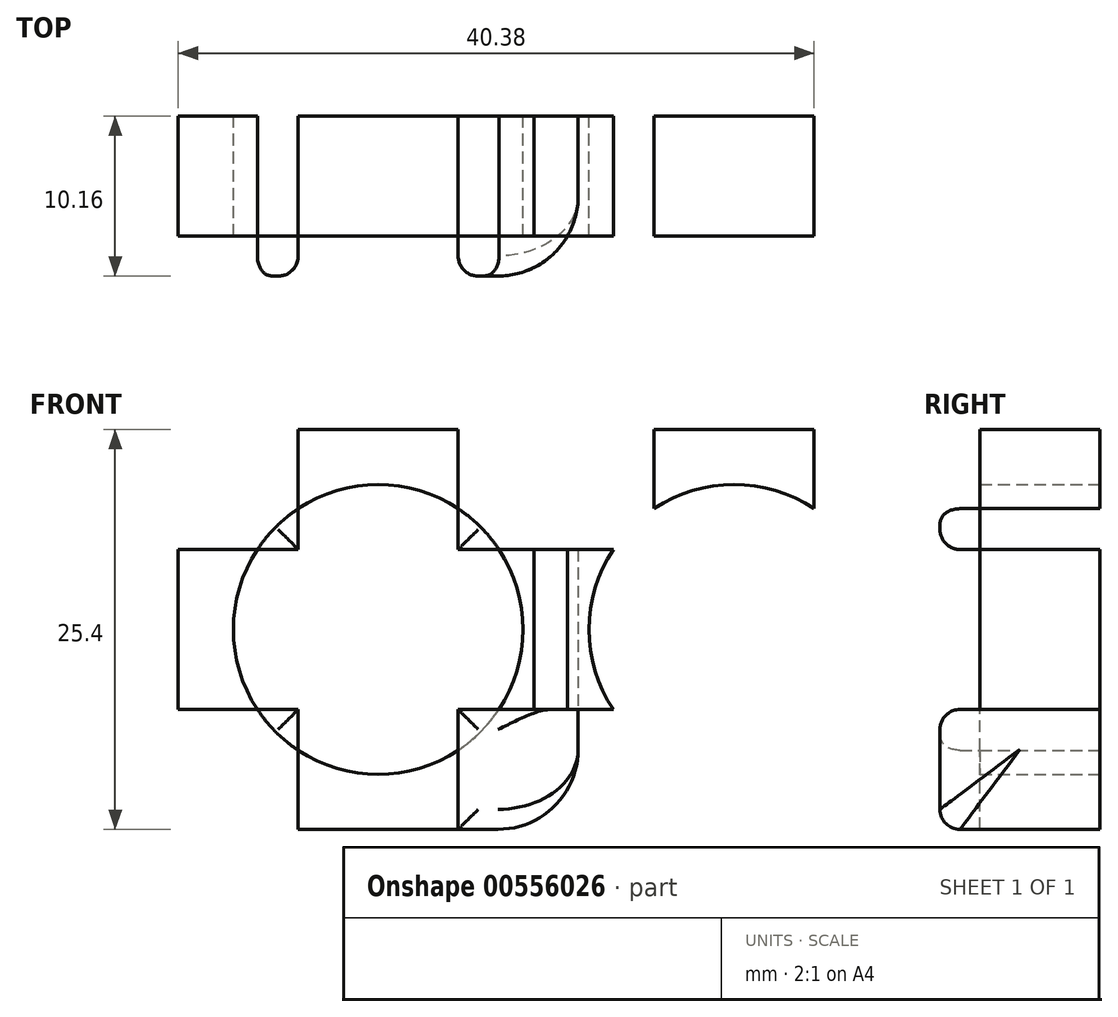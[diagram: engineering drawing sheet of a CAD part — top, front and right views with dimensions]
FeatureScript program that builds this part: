
annotation { "Feature Type Name" : "Feature", "Feature Type Description" : "" }
export const myFeature = defineFeature(function(context is Context, id is Id, definition is map)
    precondition{}
    {
        {
            var Q0;
            Q0=qCreatedBy(makeId("Front.planeOp"),FACE);
            var sketch = newSketch(context, id + "F0", { "sketchPlane" : qUnion([Q0])});
            skLineSegment(sketch, "E0.bottom", {"start": v(-53.06, 11.26) * mm, "end": v(-27.66, 11.26) * mm});
            skLineSegment(sketch, "E0.top", {"start": v(-53.06, -14.14) * mm, "end": v(-27.66, -14.14) * mm});
            skLineSegment(sketch, "E0.left", {"start": v(-53.06, 11.26) * mm, "end": v(-53.06, -14.14) * mm});
            skLineSegment(sketch, "E0.right", {"start": v(-27.66, 11.26) * mm, "end": v(-27.66, -14.14) * mm});
            skCircle(sketch, "E1", {"center": v(-40.36, -1.44) * mm, "radius": 9.2 * mm});
            skPoint(sketch, "E1.centerSnap0", {"position": v(-40.36, 11.26) * mm});
            skPoint(sketch, "E1.centerSnap1", {"position": v(-53.06, -1.44) * mm});
            skLineSegment(sketch, "E2.bottom", {"start": v(-53.06, 11.26) * mm, "end": v(-45.44, 11.26) * mm});
            skLineSegment(sketch, "E2.top", {"start": v(-53.06, 3.64) * mm, "end": v(-45.44, 3.64) * mm});
            skLineSegment(sketch, "E2.left", {"start": v(-53.06, 11.26) * mm, "end": v(-53.06, 3.64) * mm});
            skLineSegment(sketch, "E2.right", {"start": v(-45.44, 11.26) * mm, "end": v(-45.44, 3.64) * mm});
            skLineSegment(sketch, "E3", {"start": v(-40.36, 11.26) * mm, "end": v(-40.36, -16.73) * mm, "construction": true});
            skLineSegment(sketch, "E4", {"start": v(-53.06, -1.44) * mm, "end": v(-27.66, -1.44) * mm, "construction": true});
            skLineSegment(sketch, "E5.MirrorCS", {"start": v(-35.28, 11.26) * mm, "end": v(-35.28, 3.64) * mm});
            skLineSegment(sketch, "E6.MirrorCS", {"start": v(-27.66, 3.64) * mm, "end": v(-35.28, 3.64) * mm});
            skLineSegment(sketch, "E7.MirrorCS", {"start": v(-27.66, 11.26) * mm, "end": v(-27.66, 3.64) * mm});
            skLineSegment(sketch, "E8.MirrorCS", {"start": v(-27.66, 11.26) * mm, "end": v(-35.28, 11.26) * mm});
            skLineSegment(sketch, "E9.MirrorCS", {"start": v(-53.06, -14.14) * mm, "end": v(-53.06, -6.52) * mm});
            skLineSegment(sketch, "E10.MirrorCS", {"start": v(-53.06, -14.14) * mm, "end": v(-45.44, -14.14) * mm});
            skLineSegment(sketch, "E11.MirrorCS", {"start": v(-45.44, -14.14) * mm, "end": v(-45.44, -6.52) * mm});
            skLineSegment(sketch, "E12.MirrorCS", {"start": v(-53.06, -6.52) * mm, "end": v(-45.44, -6.52) * mm});
            skLineSegment(sketch, "E13.MirrorCS", {"start": v(-35.28, -14.14) * mm, "end": v(-35.28, -6.52) * mm});
            skLineSegment(sketch, "E14.MirrorCS", {"start": v(-27.66, -14.14) * mm, "end": v(-27.66, 11.26) * mm});
            skLineSegment(sketch, "E15.MirrorCS", {"start": v(-27.66, -6.52) * mm, "end": v(-35.28, -6.52) * mm});
            skSolve(sketch);
        }
        {
            var Q0;
            {var subQ4=sQuery(id+"F0.wireOp",EDGE,"E2.bottom");Q0=makeQuery(id+"F0.imprint","IMPRINT",FACE,{"disambiguationData":[TD([[makeQuery(id+"F0.imprint","IMPRINT",EDGE,{"derivedFrom":subQ4}),-1.0]])]});}
            var Q1;
            {var subQ0=sQuery(id+"F0.wireOp",EDGE,"E0.bottom");Q1=makeQuery(id+"F0.imprint","IMPRINT",FACE,{"disambiguationData":[TD([[makeQuery(id+"F0.imprint","IMPRINT",EDGE,{"derivedFrom":subQ0}),-1.0]])]});}
            var Q2;
            {var subQ0=sQuery(id+"F0.wireOp",EDGE,"E8.MirrorCS");Q2=makeQuery(id+"F0.imprint","IMPRINT",FACE,{"disambiguationData":[TD([[makeQuery(id+"F0.imprint","IMPRINT",EDGE,{"derivedFrom":subQ0}),1.0]])]});}
            var Q3;
            {var subQ0=sQuery(id+"F0.wireOp",EDGE,"E6.MirrorCS");var subQ1=sQuery(id+"F0.wireOp",EDGE,"E1");var subQ2=makeQuery(id+"F0.imprint","INTERSECT",VERTEX,{"derivedFrom":[subQ1,subQ0]});Q3=makeQuery(id+"F0.imprint","IMPRINT",FACE,{"disambiguationData":[TD([[makeQuery(id+"F0.imprint","IMPRINT",EDGE,{"disambiguationData":[TD([[subQ2,1.0]])],"derivedFrom":subQ1}),-1.0]])]});}
            var Q4;
            {var subQ1=sQuery(id+"F0.wireOp",EDGE,"E13.MirrorCS");var subQ5=sQuery(id+"F0.wireOp",EDGE,"E1");var subQ6=makeQuery(id+"F0.imprint","INTERSECT",VERTEX,{"derivedFrom":[subQ5,subQ1]});Q4=makeQuery(id+"F0.imprint","IMPRINT",FACE,{"disambiguationData":[TD([[makeQuery(id+"F0.imprint","IMPRINT",EDGE,{"disambiguationData":[TD([[subQ6,-1.0]])],"derivedFrom":subQ5}),-1.0]])]});}
            var Q5;
            {var subQ0=sQuery(id+"F0.wireOp",EDGE,"E11.MirrorCS");var subQ1=sQuery(id+"F0.wireOp",EDGE,"E1");var subQ2=makeQuery(id+"F0.imprint","INTERSECT",VERTEX,{"derivedFrom":[subQ1,subQ0]});Q5=makeQuery(id+"F0.imprint","IMPRINT",FACE,{"disambiguationData":[TD([[makeQuery(id+"F0.imprint","IMPRINT",EDGE,{"disambiguationData":[TD([[subQ2,-1.0]])],"derivedFrom":subQ1}),-1.0]])]});}
            var Q6;
            {var subQ1=sQuery(id+"F0.wireOp",EDGE,"E9.MirrorCS");Q6=makeQuery(id+"F0.imprint","IMPRINT",FACE,{"disambiguationData":[TD([[makeQuery(id+"F0.imprint","IMPRINT",EDGE,{"derivedFrom":subQ1}),-1.0]])]});}
            var Q7;
            {var subQ0=sQuery(id+"F0.wireOp",EDGE,"E0.left");Q7=makeQuery(id+"F0.imprint","IMPRINT",FACE,{"disambiguationData":[TD([[makeQuery(id+"F0.imprint","IMPRINT",EDGE,{"derivedFrom":subQ0}),1.0]])]});}
            extrude(context, id + "F1", {"entities" : qUnion([Q0, Q1, Q2, Q3, Q4, Q5, Q6, Q7]), "depth" : 7.62 * mm, "offsetDistance" : 25.4 * mm});
        }
        {
            var Q0;
            {var subQ0=sQuery(id+"F0.wireOp",EDGE,"E8.MirrorCS");Q0=makeQuery(id+"F0.imprint","IMPRINT",FACE,{"disambiguationData":[TD([[makeQuery(id+"F0.imprint","IMPRINT",EDGE,{"derivedFrom":subQ0}),1.0]])]});}
            var Q1;
            {var subQ0=sQuery(id+"F0.wireOp",EDGE,"E5.MirrorCS");var subQ1=sQuery(id+"F0.wireOp",EDGE,"E1");var subQ2=makeQuery(id+"F0.imprint","INTERSECT",VERTEX,{"derivedFrom":[subQ1,subQ0]});Q1=makeQuery(id+"F0.imprint","IMPRINT",FACE,{"disambiguationData":[TD([[makeQuery(id+"F0.imprint","IMPRINT",EDGE,{"disambiguationData":[TD([[subQ2,1.0]])],"derivedFrom":subQ1}),1.0]])]});}
            var Q2;
            {var subQ4=sQuery(id+"F0.wireOp",EDGE,"E2.bottom");Q2=makeQuery(id+"F0.imprint","IMPRINT",FACE,{"disambiguationData":[TD([[makeQuery(id+"F0.imprint","IMPRINT",EDGE,{"derivedFrom":subQ4}),-1.0]])]});}
            var Q3;
            {var subQ1=sQuery(id+"F0.wireOp",EDGE,"E9.MirrorCS");Q3=makeQuery(id+"F0.imprint","IMPRINT",FACE,{"disambiguationData":[TD([[makeQuery(id+"F0.imprint","IMPRINT",EDGE,{"derivedFrom":subQ1}),-1.0]])]});}
            var Q4;
            {var subQ0=sQuery(id+"F0.wireOp",EDGE,"E12.MirrorCS");var subQ1=sQuery(id+"F0.wireOp",EDGE,"E1");var subQ2=makeQuery(id+"F0.imprint","INTERSECT",VERTEX,{"derivedFrom":[subQ1,subQ0]});Q4=makeQuery(id+"F0.imprint","IMPRINT",FACE,{"disambiguationData":[TD([[makeQuery(id+"F0.imprint","IMPRINT",EDGE,{"disambiguationData":[TD([[subQ2,-1.0]])],"derivedFrom":subQ1}),1.0]])]});}
            var Q5;
            {var subQ0=sQuery(id+"F0.wireOp",EDGE,"E2.right");var subQ1=sQuery(id+"F0.wireOp",EDGE,"E1");var subQ2=makeQuery(id+"F0.imprint","INTERSECT",VERTEX,{"derivedFrom":[subQ1,subQ0]});Q5=makeQuery(id+"F0.imprint","IMPRINT",FACE,{"disambiguationData":[TD([[makeQuery(id+"F0.imprint","IMPRINT",EDGE,{"disambiguationData":[TD([[subQ2,-1.0]])],"derivedFrom":subQ1}),1.0]])]});}
            var Q6;
            {var subQ1=sQuery(id+"F0.wireOp",EDGE,"E13.MirrorCS");var subQ5=sQuery(id+"F0.wireOp",EDGE,"E1");var subQ6=makeQuery(id+"F0.imprint","INTERSECT",VERTEX,{"derivedFrom":[subQ5,subQ1]});Q6=makeQuery(id+"F0.imprint","IMPRINT",FACE,{"disambiguationData":[TD([[makeQuery(id+"F0.imprint","IMPRINT",EDGE,{"disambiguationData":[TD([[subQ6,-1.0]])],"derivedFrom":subQ5}),-1.0]])]});}
            var Q7;
            {var subQ0=sQuery(id+"F0.wireOp",EDGE,"E13.MirrorCS");var subQ1=sQuery(id+"F0.wireOp",EDGE,"E1");var subQ2=makeQuery(id+"F0.imprint","INTERSECT",VERTEX,{"derivedFrom":[subQ1,subQ0]});Q7=makeQuery(id+"F0.imprint","IMPRINT",FACE,{"disambiguationData":[TD([[makeQuery(id+"F0.imprint","IMPRINT",EDGE,{"disambiguationData":[TD([[subQ2,-1.0]])],"derivedFrom":subQ1}),1.0]])]});}
            extrude(context, id + "F2", {"entities" : qUnion([Q0, Q1, Q2, Q3, Q4, Q5, Q6, Q7]), "operationType" : NewBodyOperationType.ADD, "depth" : 10.16 * mm, "offsetDistance" : 25.4 * mm});
        }
        {
            var Q0;
            {var subQ0=sQuery(id+"F0.wireOp",EDGE,"E2.right");var subQ1=sQuery(id+"F0.wireOp",EDGE,"E1");var subQ2=makeQuery(id+"F0.imprint","INTERSECT",VERTEX,{"derivedFrom":[subQ1,subQ0]});Q0=makeQuery(id+"F0.imprint","IMPRINT",FACE,{"disambiguationData":[TD([[makeQuery(id+"F0.imprint","IMPRINT",EDGE,{"disambiguationData":[TD([[subQ2,-1.0]])],"derivedFrom":subQ1}),1.0]])]});}
            var Q1;
            {var subQ0=sQuery(id+"F0.wireOp",EDGE,"E12.MirrorCS");var subQ1=sQuery(id+"F0.wireOp",EDGE,"E1");var subQ2=makeQuery(id+"F0.imprint","INTERSECT",VERTEX,{"derivedFrom":[subQ1,subQ0]});Q1=makeQuery(id+"F0.imprint","IMPRINT",FACE,{"disambiguationData":[TD([[makeQuery(id+"F0.imprint","IMPRINT",EDGE,{"disambiguationData":[TD([[subQ2,-1.0]])],"derivedFrom":subQ1}),1.0]])]});}
            var Q2;
            {var subQ0=sQuery(id+"F0.wireOp",EDGE,"E13.MirrorCS");var subQ1=sQuery(id+"F0.wireOp",EDGE,"E1");var subQ2=makeQuery(id+"F0.imprint","INTERSECT",VERTEX,{"derivedFrom":[subQ1,subQ0]});Q2=makeQuery(id+"F0.imprint","IMPRINT",FACE,{"disambiguationData":[TD([[makeQuery(id+"F0.imprint","IMPRINT",EDGE,{"disambiguationData":[TD([[subQ2,-1.0]])],"derivedFrom":subQ1}),1.0]])]});}
            var Q3;
            {var subQ0=sQuery(id+"F0.wireOp",EDGE,"E5.MirrorCS");var subQ1=sQuery(id+"F0.wireOp",EDGE,"E1");var subQ2=makeQuery(id+"F0.imprint","INTERSECT",VERTEX,{"derivedFrom":[subQ1,subQ0]});Q3=makeQuery(id+"F0.imprint","IMPRINT",FACE,{"disambiguationData":[TD([[makeQuery(id+"F0.imprint","IMPRINT",EDGE,{"disambiguationData":[TD([[subQ2,1.0]])],"derivedFrom":subQ1}),1.0]])]});}
            extrude(context, id + "F3", {"entities" : qUnion([Q0, Q1, Q2, Q3]), "operationType" : NewBodyOperationType.REMOVE, "depth" : 7.62 * mm, "offsetDistance" : 25.4 * mm});
        }
        {
            var Q0;
            Q0=makeQuery(id+"F1.opExtrude","SWEPT_BODY",BODY,{"disambiguationData":[OSD([sQuery(id+"F0.wireOp",EDGE,"E0.bottom"),sQuery(id+"F0.wireOp",EDGE,"E0.left"),sQuery(id+"F0.wireOp",EDGE,"E1"),sQuery(id+"F0.wireOp",EDGE,"E2.bottom"),sQuery(id+"F0.wireOp",EDGE,"E2.left"),sQuery(id+"F0.wireOp",EDGE,"E8.MirrorCS"),sQuery(id+"F0.wireOp",EDGE,"E9.MirrorCS"),sQuery(id+"F0.wireOp",EDGE,"E0.top"),sQuery(id+"F0.wireOp",EDGE,"E14.MirrorCS")])]});
            transform(context, id + "F4", {"entities" : qUnion([Q0]), "transformType" : TransformType.TRANSLATION_3D, "dx" : 22.6 * mm, "dy" : 0 * mm, "dz" : 0 * mm, "makeCopy" : true});
        }
        {
            var Q0;
            Q0=makeQuery(id+"F1.opExtrude","SWEPT_BODY",BODY,{"disambiguationData":[OSD([sQuery(id+"F0.wireOp",EDGE,"E0.bottom"),sQuery(id+"F0.wireOp",EDGE,"E0.left"),sQuery(id+"F0.wireOp",EDGE,"E1"),sQuery(id+"F0.wireOp",EDGE,"E2.bottom"),sQuery(id+"F0.wireOp",EDGE,"E2.left"),sQuery(id+"F0.wireOp",EDGE,"E8.MirrorCS"),sQuery(id+"F0.wireOp",EDGE,"E9.MirrorCS"),sQuery(id+"F0.wireOp",EDGE,"E0.top"),sQuery(id+"F0.wireOp",EDGE,"E14.MirrorCS")])]});
            var Q1;
            Q1=makeQuery(id+"F4.opPattern","COPY",BODY,{"derivedFrom":makeQuery(id+"F1.opExtrude","SWEPT_BODY",BODY,{"disambiguationData":[OSD([sQuery(id+"F0.wireOp",EDGE,"E0.bottom"),sQuery(id+"F0.wireOp",EDGE,"E0.left"),sQuery(id+"F0.wireOp",EDGE,"E1"),sQuery(id+"F0.wireOp",EDGE,"E2.bottom"),sQuery(id+"F0.wireOp",EDGE,"E2.left"),sQuery(id+"F0.wireOp",EDGE,"E8.MirrorCS"),sQuery(id+"F0.wireOp",EDGE,"E9.MirrorCS"),sQuery(id+"F0.wireOp",EDGE,"E0.top"),sQuery(id+"F0.wireOp",EDGE,"E14.MirrorCS")])]}),"instanceName":"1"});
            booleanBodies(context, id + "F5", {"operationType" : BooleanOperationType.UNION, "tools" : qUnion([Q0, Q1])});
        }
        {
            var Q0;
            Q0=makeQuery(id+"F2.opExtrude","CAP_EDGE",EDGE,{"disambiguationData":[OSD([sQuery(id+"F0.wireOp",EDGE,"E2.bottom")])],"isStart":false});
            var Q1;
            Q1=makeQuery(id+"F2.opExtrude","CAP_EDGE",EDGE,{"disambiguationData":[OSD([sQuery(id+"F0.wireOp",EDGE,"E2.left")])],"isStart":false});
            var Q2;
            Q2=makeQuery(id+"F5.opBoolean","MERGE",EDGE,{"derivedFrom":[makeQuery(id+"F2.opExtrude","CAP_EDGE",EDGE,{"disambiguationData":[OSD([sQuery(id+"F0.wireOp",EDGE,"E8.MirrorCS")])],"isStart":false}),makeQuery(id+"F4.opPattern","COPY",EDGE,{"derivedFrom":makeQuery(id+"F2.opExtrude","CAP_EDGE",EDGE,{"disambiguationData":[OSD([sQuery(id+"F0.wireOp",EDGE,"E2.bottom")])],"isStart":false}),"instanceName":"1"})]});
            var Q3;
            Q3=makeQuery(id+"F4.opPattern","COPY",EDGE,{"derivedFrom":makeQuery(id+"F2.opExtrude","CAP_EDGE",EDGE,{"disambiguationData":[OSD([sQuery(id+"F0.wireOp",EDGE,"E8.MirrorCS")])],"isStart":false}),"instanceName":"1"});
            var Q4;
            {var subQ0=sQuery(id+"F0.wireOp",EDGE,"E14.MirrorCS");Q4=makeQuery(id+"F4.opPattern","COPY",EDGE,{"derivedFrom":makeQuery(id+"F2.opExtrude","CAP_EDGE",EDGE,{"disambiguationData":[OSD([subQ0]),TDD([makeQuery(id+"F0.imprint","IMPRINT",EDGE,{"disambiguationData":[TD([[makeQuery(id+"F0.imprint","INTERSECT",VERTEX,{"derivedFrom":[sQuery(id+"F0.wireOp",EDGE,"E6.MirrorCS"),subQ0]}),-1.0]])],"derivedFrom":subQ0})])],"isStart":false}),"instanceName":"1"});}
            var Q5;
            {var subQ0=sQuery(id+"F0.wireOp",EDGE,"E14.MirrorCS");Q5=makeQuery(id+"F4.opPattern","COPY",EDGE,{"derivedFrom":makeQuery(id+"F2.opExtrude","CAP_EDGE",EDGE,{"disambiguationData":[OSD([subQ0]),TDD([makeQuery(id+"F0.imprint","IMPRINT",EDGE,{"disambiguationData":[TD([[makeQuery(id+"F0.imprint","INTERSECT",VERTEX,{"derivedFrom":[sQuery(id+"F0.wireOp",EDGE,"E0.top"),subQ0]}),-1.0]])],"derivedFrom":subQ0})])],"isStart":false}),"instanceName":"1"});}
            var Q6;
            {var subQ0=sQuery(id+"F0.wireOp",EDGE,"E0.top");Q6=makeQuery(id+"F4.opPattern","COPY",EDGE,{"derivedFrom":makeQuery(id+"F2.opExtrude","CAP_EDGE",EDGE,{"disambiguationData":[OSD([subQ0]),TDD([makeQuery(id+"F0.imprint","IMPRINT",EDGE,{"disambiguationData":[TD([[makeQuery(id+"F0.imprint","INTERSECT",VERTEX,{"derivedFrom":[sQuery(id+"F0.wireOp",EDGE,"E13.MirrorCS"),subQ0]}),-1.0]])],"derivedFrom":subQ0})])],"isStart":false}),"instanceName":"1"});}
            var Q7;
            {var subQ0=sQuery(id+"F0.wireOp",EDGE,"E0.top");Q7=makeQuery(id+"F5.opBoolean","MERGE",EDGE,{"derivedFrom":[makeQuery(id+"F2.opExtrude","CAP_EDGE",EDGE,{"disambiguationData":[OSD([subQ0]),TDD([makeQuery(id+"F0.imprint","IMPRINT",EDGE,{"disambiguationData":[TD([[makeQuery(id+"F0.imprint","INTERSECT",VERTEX,{"derivedFrom":[sQuery(id+"F0.wireOp",EDGE,"E13.MirrorCS"),subQ0]}),-1.0]])],"derivedFrom":subQ0})])],"isStart":false}),makeQuery(id+"F4.opPattern","COPY",EDGE,{"derivedFrom":makeQuery(id+"F2.opExtrude","CAP_EDGE",EDGE,{"disambiguationData":[OSD([subQ0]),TDD([makeQuery(id+"F0.imprint","IMPRINT",EDGE,{"disambiguationData":[TD([[makeQuery(id+"F0.imprint","INTERSECT",VERTEX,{"derivedFrom":[sQuery(id+"F0.wireOp",EDGE,"E9.MirrorCS"),subQ0]}),-1.0]])],"derivedFrom":subQ0})])],"isStart":false}),"instanceName":"1"})]});}
            var Q8;
            {var subQ0=sQuery(id+"F0.wireOp",EDGE,"E0.top");Q8=makeQuery(id+"F2.opExtrude","CAP_EDGE",EDGE,{"disambiguationData":[OSD([subQ0]),TDD([makeQuery(id+"F0.imprint","IMPRINT",EDGE,{"disambiguationData":[TD([[makeQuery(id+"F0.imprint","INTERSECT",VERTEX,{"derivedFrom":[sQuery(id+"F0.wireOp",EDGE,"E9.MirrorCS"),subQ0]}),-1.0]])],"derivedFrom":subQ0})])],"isStart":false});}
            var Q9;
            Q9=makeQuery(id+"F2.opExtrude","CAP_EDGE",EDGE,{"disambiguationData":[OSD([sQuery(id+"F0.wireOp",EDGE,"E9.MirrorCS")])],"isStart":false});
            var Q10;
            Q10=makeQuery(id+"F2.opExtrude","CAP_EDGE",EDGE,{"disambiguationData":[OSD([sQuery(id+"F0.wireOp",EDGE,"E2.top")])],"isStart":false});
            var Q11;
            Q11=makeQuery(id+"F2.opExtrude","CAP_EDGE",EDGE,{"disambiguationData":[OSD([sQuery(id+"F0.wireOp",EDGE,"E2.right")])],"isStart":false});
            var Q12;
            Q12=makeQuery(id+"F2.opExtrude","CAP_EDGE",EDGE,{"disambiguationData":[OSD([sQuery(id+"F0.wireOp",EDGE,"E5.MirrorCS")])],"isStart":false});
            var Q13;
            Q13=makeQuery(id+"F5.opBoolean","MERGE",EDGE,{"derivedFrom":[makeQuery(id+"F2.opExtrude","CAP_EDGE",EDGE,{"disambiguationData":[OSD([sQuery(id+"F0.wireOp",EDGE,"E6.MirrorCS")])],"isStart":false}),makeQuery(id+"F4.opPattern","COPY",EDGE,{"derivedFrom":makeQuery(id+"F2.opExtrude","CAP_EDGE",EDGE,{"disambiguationData":[OSD([sQuery(id+"F0.wireOp",EDGE,"E2.top")])],"isStart":false}),"instanceName":"1"})]});
            var Q14;
            Q14=makeQuery(id+"F4.opPattern","COPY",EDGE,{"derivedFrom":makeQuery(id+"F2.opExtrude","CAP_EDGE",EDGE,{"disambiguationData":[OSD([sQuery(id+"F0.wireOp",EDGE,"E2.right")])],"isStart":false}),"instanceName":"1"});
            var Q15;
            Q15=makeQuery(id+"F4.opPattern","COPY",EDGE,{"derivedFrom":makeQuery(id+"F2.opExtrude","CAP_EDGE",EDGE,{"disambiguationData":[OSD([sQuery(id+"F0.wireOp",EDGE,"E6.MirrorCS")])],"isStart":false}),"instanceName":"1"});
            var Q16;
            Q16=makeQuery(id+"F4.opPattern","COPY",EDGE,{"derivedFrom":makeQuery(id+"F2.opExtrude","CAP_EDGE",EDGE,{"disambiguationData":[OSD([sQuery(id+"F0.wireOp",EDGE,"E5.MirrorCS")])],"isStart":false}),"instanceName":"1"});
            var Q17;
            Q17=makeQuery(id+"F4.opPattern","COPY",EDGE,{"derivedFrom":makeQuery(id+"F2.opExtrude","CAP_EDGE",EDGE,{"disambiguationData":[OSD([sQuery(id+"F0.wireOp",EDGE,"E15.MirrorCS")])],"isStart":false}),"instanceName":"1"});
            var Q18;
            Q18=makeQuery(id+"F4.opPattern","COPY",EDGE,{"derivedFrom":makeQuery(id+"F2.opExtrude","CAP_EDGE",EDGE,{"disambiguationData":[OSD([sQuery(id+"F0.wireOp",EDGE,"E13.MirrorCS")])],"isStart":false}),"instanceName":"1"});
            var Q19;
            Q19=makeQuery(id+"F4.opPattern","COPY",EDGE,{"derivedFrom":makeQuery(id+"F2.opExtrude","CAP_EDGE",EDGE,{"disambiguationData":[OSD([sQuery(id+"F0.wireOp",EDGE,"E11.MirrorCS")])],"isStart":false}),"instanceName":"1"});
            var Q20;
            Q20=makeQuery(id+"F2.opExtrude","CAP_EDGE",EDGE,{"disambiguationData":[OSD([sQuery(id+"F0.wireOp",EDGE,"E13.MirrorCS")])],"isStart":false});
            var Q21;
            Q21=makeQuery(id+"F5.opBoolean","MERGE",EDGE,{"derivedFrom":[makeQuery(id+"F2.opExtrude","CAP_EDGE",EDGE,{"disambiguationData":[OSD([sQuery(id+"F0.wireOp",EDGE,"E15.MirrorCS")])],"isStart":false}),makeQuery(id+"F4.opPattern","COPY",EDGE,{"derivedFrom":makeQuery(id+"F2.opExtrude","CAP_EDGE",EDGE,{"disambiguationData":[OSD([sQuery(id+"F0.wireOp",EDGE,"E12.MirrorCS")])],"isStart":false}),"instanceName":"1"})]});
            var Q22;
            Q22=makeQuery(id+"F2.opExtrude","CAP_EDGE",EDGE,{"disambiguationData":[OSD([sQuery(id+"F0.wireOp",EDGE,"E11.MirrorCS")])],"isStart":false});
            var Q23;
            Q23=makeQuery(id+"F2.opExtrude","CAP_EDGE",EDGE,{"disambiguationData":[OSD([sQuery(id+"F0.wireOp",EDGE,"E12.MirrorCS")])],"isStart":false});
            fillet(context, id + "F6", {"entities" : qUnion([Q0, Q1, Q2, Q3, Q4, Q5, Q6, Q7, Q8, Q9, Q10, Q11, Q12, Q13, Q14, Q15, Q16, Q17, Q18, Q19, Q20, Q21, Q22, Q23]), "radius" : 1.27 * mm, "tangentPropagation" : true, "allowEdgeOverflow" : false});
        }
        {
            var Q0;
            {var subQ0=sQuery(id+"F0.wireOp",EDGE,"E14.MirrorCS");var subQ1=sQuery(id+"F0.wireOp",EDGE,"E8.MirrorCS");Q0=makeQuery(id+"F4.opPattern","COPY",EDGE,{"derivedFrom":makeQuery(id+"F2.boolean.opBoolean","MERGE",EDGE,{"derivedFrom":[makeQuery(id+"F1.opExtrude","SWEPT_EDGE",EDGE,{"disambiguationData":[OSD([subQ1,subQ0])]}),makeQuery(id+"F2.opExtrude","SWEPT_EDGE",EDGE,{"disambiguationData":[OSD([subQ1,subQ0])]})]}),"instanceName":"1"});}
            var Q1;
            {var subQ0=sQuery(id+"F0.wireOp",EDGE,"E14.MirrorCS");var subQ1=sQuery(id+"F0.wireOp",EDGE,"E0.top");Q1=makeQuery(id+"F4.opPattern","COPY",EDGE,{"derivedFrom":makeQuery(id+"F2.boolean.opBoolean","MERGE",EDGE,{"derivedFrom":[makeQuery(id+"F1.opExtrude","SWEPT_EDGE",EDGE,{"disambiguationData":[OSD([subQ1,subQ0])]}),makeQuery(id+"F2.opExtrude","SWEPT_EDGE",EDGE,{"disambiguationData":[OSD([subQ1,subQ0])]})]}),"instanceName":"1"});}
            var Q2;
            {var subQ0=sQuery(id+"F0.wireOp",EDGE,"E2.left");var subQ1=sQuery(id+"F0.wireOp",EDGE,"E2.bottom");Q2=makeQuery(id+"F2.boolean.opBoolean","MERGE",EDGE,{"derivedFrom":[makeQuery(id+"F1.opExtrude","SWEPT_EDGE",EDGE,{"disambiguationData":[OSD([subQ1,subQ0])]}),makeQuery(id+"F2.opExtrude","SWEPT_EDGE",EDGE,{"disambiguationData":[OSD([subQ1,subQ0])]})]});}
            var Q3;
            {var subQ0=sQuery(id+"F0.wireOp",EDGE,"E0.top");var subQ1=sQuery(id+"F0.wireOp",EDGE,"E9.MirrorCS");Q3=makeQuery(id+"F2.boolean.opBoolean","MERGE",EDGE,{"derivedFrom":[makeQuery(id+"F1.opExtrude","SWEPT_EDGE",EDGE,{"disambiguationData":[OSD([subQ1,subQ0])]}),makeQuery(id+"F2.opExtrude","SWEPT_EDGE",EDGE,{"disambiguationData":[OSD([subQ1,subQ0])]})]});}
            fillet(context, id + "F7", {"entities" : qUnion([Q0, Q1, Q2, Q3]), "radius" : 5.08 * mm, "tangentPropagation" : true, "allowEdgeOverflow" : false});
        }
    });
